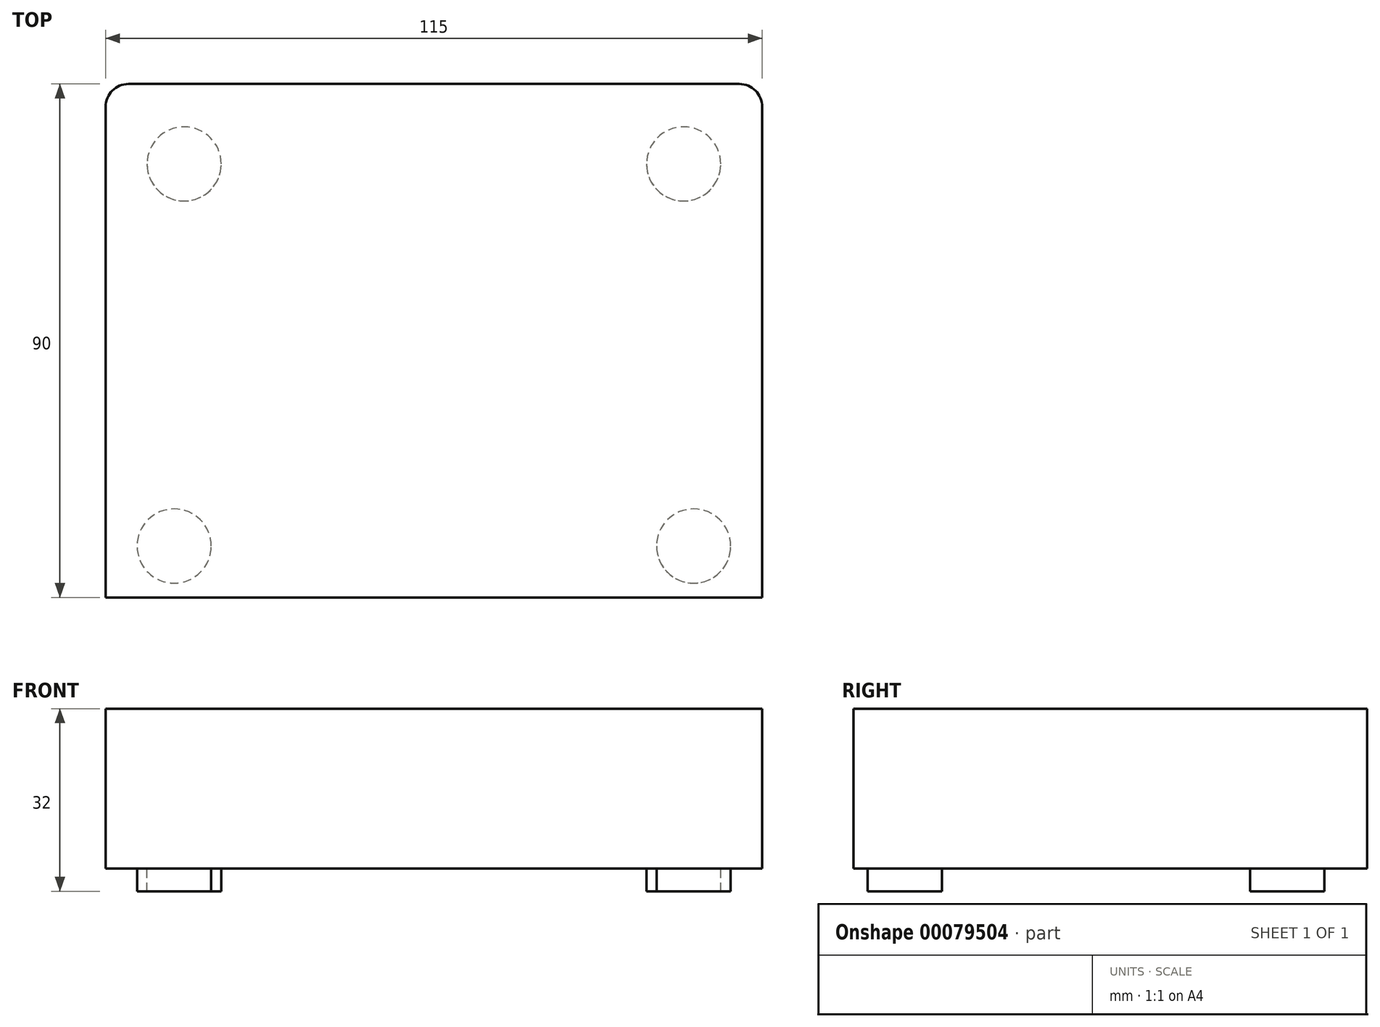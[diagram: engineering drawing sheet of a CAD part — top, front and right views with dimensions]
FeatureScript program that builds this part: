
annotation { "Feature Type Name" : "Feature", "Feature Type Description" : "" }
export const myFeature = defineFeature(function(context is Context, id is Id, definition is map)
    precondition{}
    {
        {
            var Q0;
            Q0=qCreatedBy(makeId("Top.planeOp"),FACE);
            var sketch = newSketch(context, id + "F0", { "sketchPlane" : qUnion([Q0])});
            skLineSegment(sketch, "E0.bottom", {"start": v(-53.5, 90) * mm, "end": v(53.5, 90) * mm});
            skLineSegment(sketch, "E0.top", {"start": v(-57.5, 0) * mm, "end": v(57.5, 0) * mm});
            skLineSegment(sketch, "E0.left", {"start": v(-57.5, 86) * mm, "end": v(-57.5, 0) * mm});
            skLineSegment(sketch, "E0.right", {"start": v(57.5, 86) * mm, "end": v(57.5, 0) * mm});
            skPoint(sketch, "E1.visualSharp", {"position": v(-57.5, 90) * mm});
            skArc(sketch, "E1.filletArc", {"start": v(-53.5, 90) * mm, "mid": v(-56.33, 88.83) * mm, "end": v(-57.5, 86) * mm});
            skPoint(sketch, "E2.visualSharp", {"position": v(57.5, 90) * mm});
            skArc(sketch, "E2.filletArc", {"start": v(57.5, 86) * mm, "mid": v(56.33, 88.83) * mm, "end": v(53.5, 90) * mm});
            skSolve(sketch);
        }
        {
            var Q0;
            Q0=makeQuery(id+"F0.imprint","IMPRINT",FACE,{"disambiguationData":[TD([[makeQuery(id+"F0.imprint","IMPRINT",EDGE,{"derivedFrom":sQuery(id+"F0.wireOp",EDGE,"E0.bottom")}),-1.0]])]});
            extrude(context, id + "F1", {"entities" : qUnion([Q0]), "depth" : 28 * mm});
        }
        {
            var Q0;
            Q0=makeQuery(id+"F1.opExtrude","CAP_FACE",FACE,{"disambiguationData":[OSD([sQuery(id+"F0.wireOp",EDGE,"E0.bottom"),sQuery(id+"F0.wireOp",EDGE,"E0.top"),sQuery(id+"F0.wireOp",EDGE,"E0.left"),sQuery(id+"F0.wireOp",EDGE,"E0.right"),sQuery(id+"F0.wireOp",EDGE,"E1.filletArc"),sQuery(id+"F0.wireOp",EDGE,"E2.filletArc")])],"isStart":true});
            var sketch = newSketch(context, id + "F2", { "sketchPlane" : qUnion([Q0])});
            skCircle(sketch, "E3", {"center": v(-45.5, -9) * mm, "radius": 6.5 * mm});
            skCircle(sketch, "E4", {"center": v(-43.75, -75.98) * mm, "radius": 6.5 * mm});
            skCircle(sketch, "E5.MirrorC", {"center": v(45.5, -9) * mm, "radius": 6.5 * mm});
            skCircle(sketch, "E6.MirrorC", {"center": v(43.75, -75.98) * mm, "radius": 6.5 * mm});
            skSolve(sketch);
        }
        {
            var Q0;
            Q0 = qSketchRegion(id + "F2", true);
            extrude(context, id + "F3", {"entities" : qUnion([Q0]), "operationType" : NewBodyOperationType.ADD, "depth" : 4 * mm});
        }
    });
